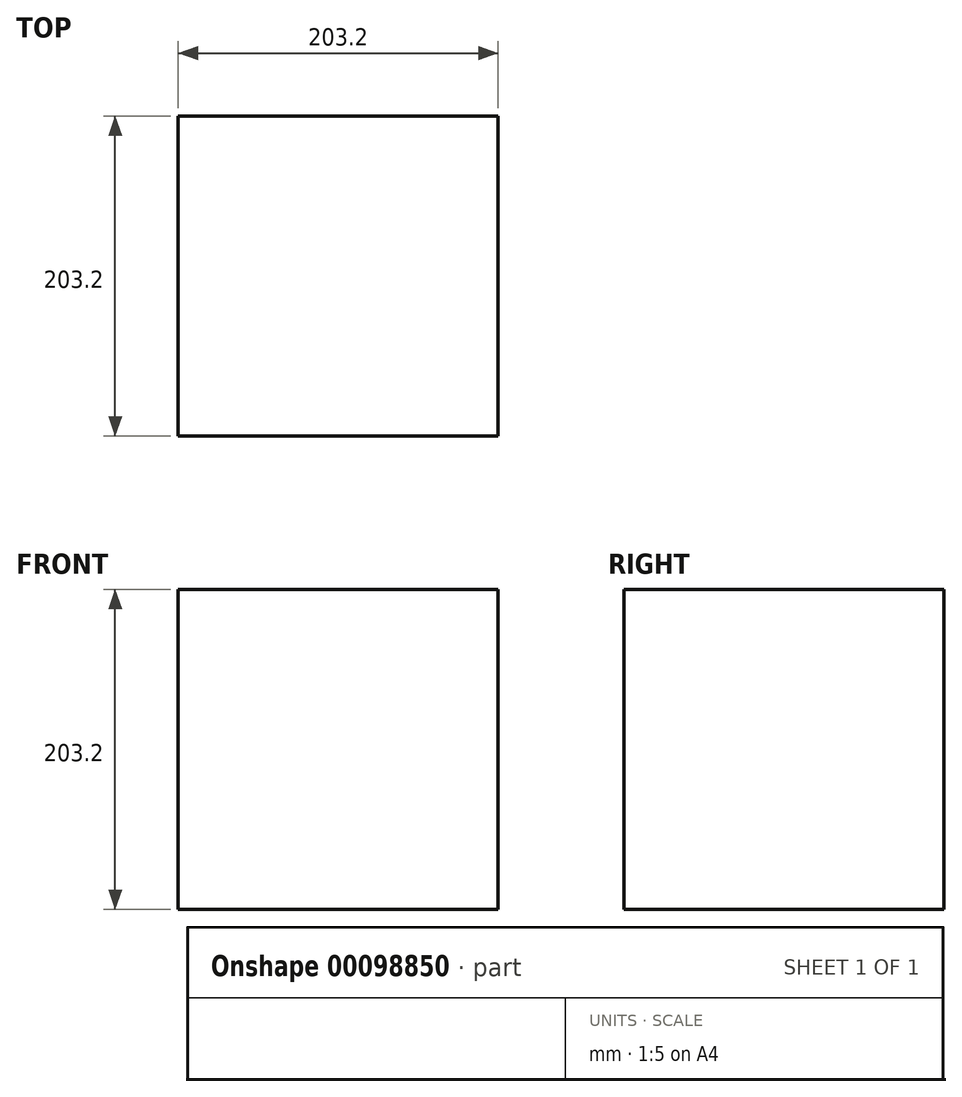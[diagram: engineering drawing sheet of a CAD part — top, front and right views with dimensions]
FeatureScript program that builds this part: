
annotation { "Feature Type Name" : "Feature", "Feature Type Description" : "" }
export const myFeature = defineFeature(function(context is Context, id is Id, definition is map)
    precondition{}
    {
        {
            var Q0;
            Q0=qCreatedBy(makeId("Front.planeOp"),FACE);
            var sketch = newSketch(context, id + "F0", { "sketchPlane" : qUnion([Q0])});
            skLineSegment(sketch, "E0.bottom", {"start": v(101.6, 101.6) * mm, "end": v(-101.6, 101.6) * mm});
            skLineSegment(sketch, "E0.top", {"start": v(101.6, -101.6) * mm, "end": v(-101.6, -101.6) * mm});
            skLineSegment(sketch, "E0.left", {"start": v(101.6, 101.6) * mm, "end": v(101.6, -101.6) * mm});
            skLineSegment(sketch, "E0.right", {"start": v(-101.6, 101.6) * mm, "end": v(-101.6, -101.6) * mm});
            skPoint(sketch, "E0.middle", {"position": v(0, 0) * mm});
            skSolve(sketch);
        }
        {
            var Q0;
            Q0 = qSketchRegion(id + "F0", true);
            extrude(context, id + "F1", {"entities" : qUnion([Q0]), "endBound" : BoundingType.SYMMETRIC, "depth" : 203.2 * mm});
        }
    });
